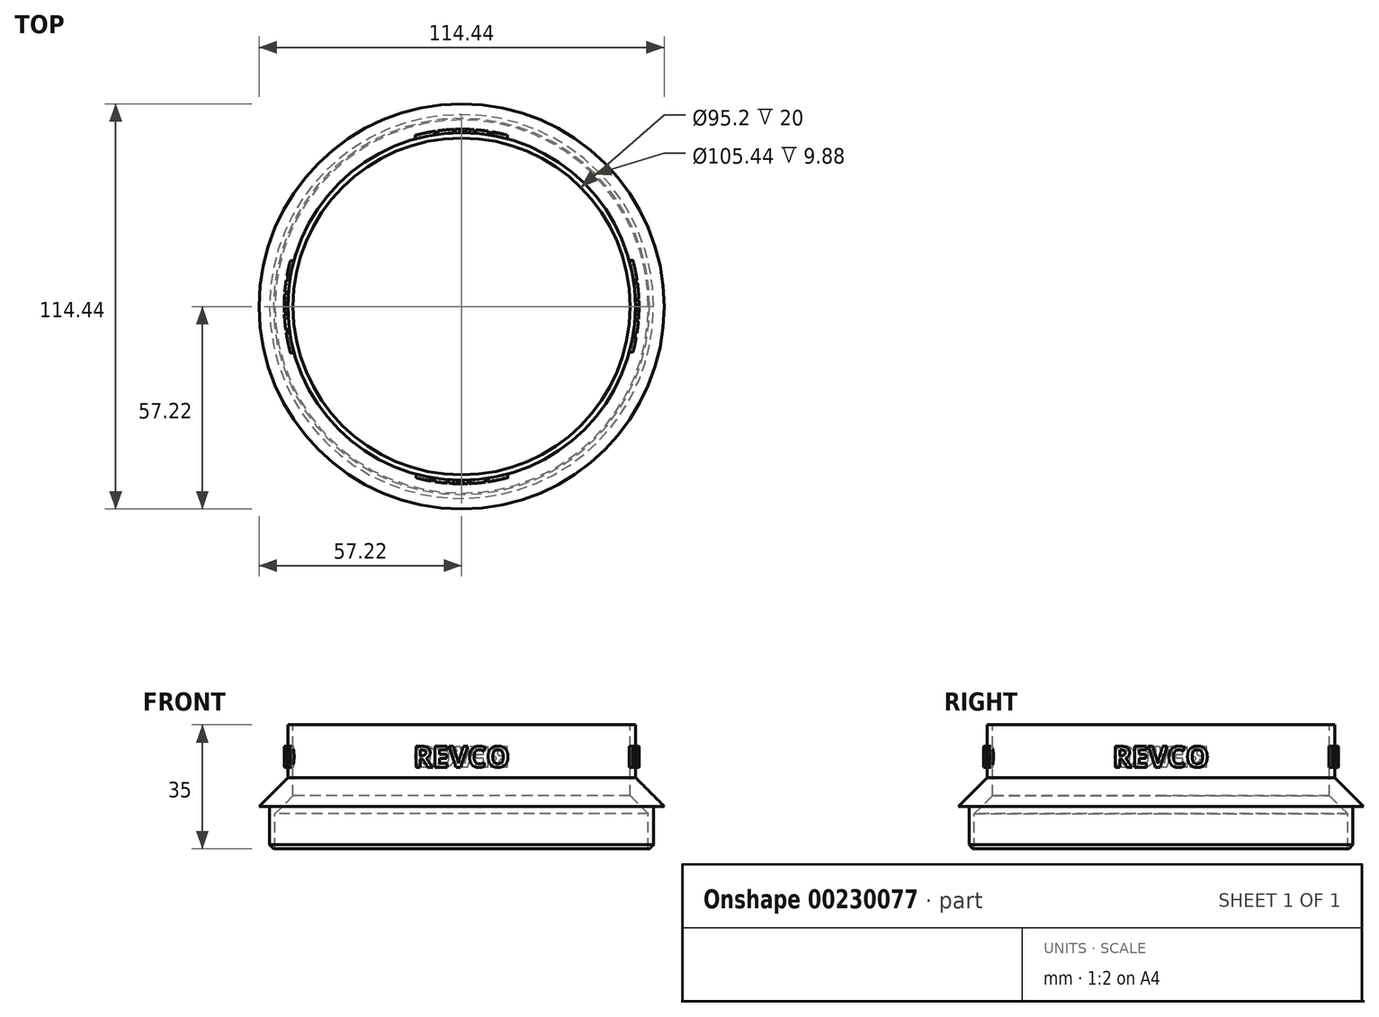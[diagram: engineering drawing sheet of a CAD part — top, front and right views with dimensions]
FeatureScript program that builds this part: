
annotation { "Feature Type Name" : "Feature", "Feature Type Description" : "" }
export const myFeature = defineFeature(function(context is Context, id is Id, definition is map)
    precondition{}
    {
        {
            var Q0;
            Q0=qCreatedBy(makeId("Front.planeOp"),FACE);
            var sketch = newSketch(context, id + "F0", { "sketchPlane" : qUnion([Q0])});
            skLineSegment(sketch, "E0", {"start": v(0, 55.93) * mm, "end": v(0, -56.28) * mm, "construction": true});
            skLineSegment(sketch, "E1.bottom", {"start": v(47.6, 20) * mm, "end": v(49.1, 20) * mm});
            skLineSegment(sketch, "E1.top", {"start": v(47.6, 0) * mm, "end": v(49.1, 0) * mm});
            skLineSegment(sketch, "E1.left", {"start": v(47.6, 20) * mm, "end": v(47.6, 0) * mm});
            skLineSegment(sketch, "E1.right", {"start": v(49.1, 20) * mm, "end": v(49.1, 0) * mm});
            skLineSegment(sketch, "E2.bottom", {"start": v(52.72, 0) * mm, "end": v(54.22, 0) * mm});
            skLineSegment(sketch, "E2.top", {"start": v(52.72, -15) * mm, "end": v(54.22, -15) * mm});
            skLineSegment(sketch, "E2.left", {"start": v(52.72, 0) * mm, "end": v(52.72, -15) * mm});
            skLineSegment(sketch, "E2.right", {"start": v(54.22, 0) * mm, "end": v(54.22, -15) * mm});
            skLineSegment(sketch, "E3", {"start": v(47.6, 0) * mm, "end": v(52.72, -5.12) * mm});
            skLineSegment(sketch, "E4", {"start": v(49.1, 5.12) * mm, "end": v(54.22, 0) * mm});
            skLineSegment(sketch, "E5", {"start": v(54.22, 0) * mm, "end": v(57.22, -3) * mm});
            skLineSegment(sketch, "E6", {"start": v(57.22, -3) * mm, "end": v(54.22, -3) * mm});
            skLineSegment(sketch, "E7", {"start": v(50.1, 18.25) * mm, "end": v(50.1, 5.74) * mm});
            skSolve(sketch);
        }
        {
            var Q0;
            {var subQ1=sQuery(id+"F0.wireOp",EDGE,"E1.bottom");Q0=makeQuery(id+"F0.imprint","IMPRINT",FACE,{"disambiguationData":[TD([[makeQuery(id+"F0.imprint","IMPRINT",EDGE,{"derivedFrom":subQ1}),-1.0]])]});}
            var Q1;
            {var subQ0=sQuery(id+"F0.wireOp",EDGE,"E5");Q1=makeQuery(id+"F0.imprint","IMPRINT",FACE,{"disambiguationData":[TD([[makeQuery(id+"F0.imprint","IMPRINT",EDGE,{"derivedFrom":subQ0}),-1.0]])]});}
            var Q2;
            {var subQ5=sQuery(id+"F0.wireOp",EDGE,"E1.top");Q2=makeQuery(id+"F0.imprint","IMPRINT",FACE,{"disambiguationData":[TD([[makeQuery(id+"F0.imprint","IMPRINT",EDGE,{"derivedFrom":subQ5}),-1.0]])]});}
            var Q3;
            {var subQ3=sQuery(id+"F0.wireOp",EDGE,"E2.bottom");Q3=makeQuery(id+"F0.imprint","IMPRINT",FACE,{"disambiguationData":[TD([[makeQuery(id+"F0.imprint","IMPRINT",EDGE,{"derivedFrom":subQ3}),-1.0]])]});}
            var Q4;
            Q4=sQuery(id+"F0.wireOp",EDGE,"E0");
            revolve(context, id + "F1", {"entities" : qUnion([Q0, Q1, Q2, Q3]), "axis" : qUnion([Q4]), "revolveType" : RevolveType.FULL});
        }
        {
            var Q0;
            Q0=makeQuery(id+"F1.opRevolve","SWEPT_EDGE",EDGE,{"disambiguationData":[OSD([sQuery(id+"F0.wireOp",EDGE,"E2.top"),sQuery(id+"F0.wireOp",EDGE,"E2.right")])]});
            chamfer(context, id + "F2", {"entities" : qUnion([Q0]), "width" : 1.1 * mm, "tangentPropagation" : true});
        }
        {
            var Q0;
            Q0 = qSketchRegion(id + "F0", true);
            var Q1;
            Q1=sQuery(id+"F0.wireOp",EDGE,"E7");
            var Q2;
            Q2=sQuery(id+"F0.wireOp",EDGE,"E0");
            revolve(context, id + "F3", {"bodyType" : ToolBodyType.SURFACE, "entities" : qUnion([Q0]), "surfaceEntities" : qUnion([Q1]), "axis" : qUnion([Q2]), "revolveType" : RevolveType.SYMMETRIC, "angle" : 1 * degree});
        }
        {
            var Q0;
            Q0=qCreatedBy(makeId("Right.planeOp"),FACE);
            cPlane(context, id + "F4", {"entities" : qUnion([Q0]), "cplaneType" : CPlaneType.OFFSET, "offset" : 60 * mm, "width" : 150 * mm, "height" : 150 * mm});
        }
        {
            var Q0;
            Q0=qCreatedBy(id+"F4.planeOp",FACE);
            var sketch = newSketch(context, id + "F5", { "sketchPlane" : qUnion([Q0])});
            skText(sketch, "E8", { "text": "REVCO", "fontName": "OpenSans-Bold.ttf"});
            const initialGuessF5  = {"E8": [-0.01364, 0.00805, 1, 0, 0.00593]};
            skSetInitialGuess(sketch, initialGuessF5);
            skSolve(sketch);
        }
        {
            var Q0;
            Q0 = qSketchRegion(id + "F5", true);
            var Q1;
            Q1=makeQuery(id+"F1.opRevolve","SWEPT_FACE",FACE,{"disambiguationData":[OSD([sQuery(id+"F0.wireOp",EDGE,"E1.right")])]});
            var Q2;
            Q2=makeQuery(id+"F3.opRevolve","SWEPT_FACE",FACE,{"disambiguationData":[OSD([sQuery(id+"F0.wireOp",EDGE,"E7")])]});
            extrude(context, id + "F6", {"entities" : qUnion([Q0]), "endBound" : BoundingType.UP_TO_SURFACE, "oppositeDirection" : true, "endBoundEntityFace" : qUnion([Q1]), "depth" : 25 * mm, "hasSecondDirection" : true, "secondDirectionBound" : SecondDirectionBoundingType.UP_TO_SURFACE, "secondDirectionOppositeDirection" : true, "secondDirectionBoundEntityFace" : qUnion([Q2]), "secondDirectionDepth" : 25 * mm});
        }
        {
            var Q0;
            Q0=makeQuery(id+"F6.opExtrude","SWEPT_BODY",BODY,{"disambiguationData":[OSD([sQuery(id+"F5.wireOp",EDGE,"E8.sketch_text.stroke-0"),sQuery(id+"F5.wireOp",EDGE,"E8.sketch_text.stroke-1"),sQuery(id+"F5.wireOp",EDGE,"E8.sketch_text.stroke-2"),sQuery(id+"F5.wireOp",EDGE,"E8.sketch_text.stroke-3"),sQuery(id+"F5.wireOp",EDGE,"E8.sketch_text.stroke-4"),sQuery(id+"F5.wireOp",EDGE,"E8.sketch_text.stroke-5"),sQuery(id+"F5.wireOp",EDGE,"E8.sketch_text.stroke-6"),sQuery(id+"F5.wireOp",EDGE,"E8.sketch_text.stroke-7"),sQuery(id+"F5.wireOp",EDGE,"E8.sketch_text.stroke-8"),sQuery(id+"F5.wireOp",EDGE,"E8.sketch_text.stroke-9"),sQuery(id+"F5.wireOp",EDGE,"E8.sketch_text.stroke-10"),sQuery(id+"F5.wireOp",EDGE,"E8.sketch_text.stroke-11"),sQuery(id+"F5.wireOp",EDGE,"E8.sketch_text.stroke-12"),sQuery(id+"F5.wireOp",EDGE,"E8.sketch_text.stroke-13"),sQuery(id+"F5.wireOp",EDGE,"E8.sketch_text.stroke-14"),sQuery(id+"F5.wireOp",EDGE,"E8.sketch_text.stroke-15"),sQuery(id+"F5.wireOp",EDGE,"E8.sketch_text.stroke-16"),sQuery(id+"F5.wireOp",EDGE,"E8.sketch_text.stroke-17"),sQuery(id+"F5.wireOp",EDGE,"E8.sketch_text.stroke-18")])]});
            var Q1;
            Q1=makeQuery(id+"F6.opExtrude","SWEPT_BODY",BODY,{"disambiguationData":[OSD([sQuery(id+"F5.wireOp",EDGE,"E8.sketch_text.stroke-19"),sQuery(id+"F5.wireOp",EDGE,"E8.sketch_text.stroke-20"),sQuery(id+"F5.wireOp",EDGE,"E8.sketch_text.stroke-21"),sQuery(id+"F5.wireOp",EDGE,"E8.sketch_text.stroke-22"),sQuery(id+"F5.wireOp",EDGE,"E8.sketch_text.stroke-23"),sQuery(id+"F5.wireOp",EDGE,"E8.sketch_text.stroke-24"),sQuery(id+"F5.wireOp",EDGE,"E8.sketch_text.stroke-25"),sQuery(id+"F5.wireOp",EDGE,"E8.sketch_text.stroke-26"),sQuery(id+"F5.wireOp",EDGE,"E8.sketch_text.stroke-27"),sQuery(id+"F5.wireOp",EDGE,"E8.sketch_text.stroke-28"),sQuery(id+"F5.wireOp",EDGE,"E8.sketch_text.stroke-29"),sQuery(id+"F5.wireOp",EDGE,"E8.sketch_text.stroke-30")])]});
            var Q2;
            Q2=makeQuery(id+"F6.opExtrude","SWEPT_BODY",BODY,{"disambiguationData":[OSD([sQuery(id+"F5.wireOp",EDGE,"E8.sketch_text.stroke-31"),sQuery(id+"F5.wireOp",EDGE,"E8.sketch_text.stroke-32"),sQuery(id+"F5.wireOp",EDGE,"E8.sketch_text.stroke-33"),sQuery(id+"F5.wireOp",EDGE,"E8.sketch_text.stroke-34"),sQuery(id+"F5.wireOp",EDGE,"E8.sketch_text.stroke-35"),sQuery(id+"F5.wireOp",EDGE,"E8.sketch_text.stroke-36"),sQuery(id+"F5.wireOp",EDGE,"E8.sketch_text.stroke-37"),sQuery(id+"F5.wireOp",EDGE,"E8.sketch_text.stroke-38"),sQuery(id+"F5.wireOp",EDGE,"E8.sketch_text.stroke-39"),sQuery(id+"F5.wireOp",EDGE,"E8.sketch_text.stroke-40")])]});
            var Q3;
            Q3=makeQuery(id+"F6.opExtrude","SWEPT_BODY",BODY,{"disambiguationData":[OSD([sQuery(id+"F5.wireOp",EDGE,"E8.sketch_text.stroke-41"),sQuery(id+"F5.wireOp",EDGE,"E8.sketch_text.stroke-42"),sQuery(id+"F5.wireOp",EDGE,"E8.sketch_text.stroke-43"),sQuery(id+"F5.wireOp",EDGE,"E8.sketch_text.stroke-44"),sQuery(id+"F5.wireOp",EDGE,"E8.sketch_text.stroke-45"),sQuery(id+"F5.wireOp",EDGE,"E8.sketch_text.stroke-46"),sQuery(id+"F5.wireOp",EDGE,"E8.sketch_text.stroke-47"),sQuery(id+"F5.wireOp",EDGE,"E8.sketch_text.stroke-48"),sQuery(id+"F5.wireOp",EDGE,"E8.sketch_text.stroke-49"),sQuery(id+"F5.wireOp",EDGE,"E8.sketch_text.stroke-50"),sQuery(id+"F5.wireOp",EDGE,"E8.sketch_text.stroke-51"),sQuery(id+"F5.wireOp",EDGE,"E8.sketch_text.stroke-52"),sQuery(id+"F5.wireOp",EDGE,"E8.sketch_text.stroke-53"),sQuery(id+"F5.wireOp",EDGE,"E8.sketch_text.stroke-54"),sQuery(id+"F5.wireOp",EDGE,"E8.sketch_text.stroke-55")])]});
            var Q4;
            Q4=makeQuery(id+"F6.opExtrude","SWEPT_BODY",BODY,{"disambiguationData":[OSD([sQuery(id+"F5.wireOp",EDGE,"E8.sketch_text.stroke-56"),sQuery(id+"F5.wireOp",EDGE,"E8.sketch_text.stroke-57"),sQuery(id+"F5.wireOp",EDGE,"E8.sketch_text.stroke-58"),sQuery(id+"F5.wireOp",EDGE,"E8.sketch_text.stroke-59"),sQuery(id+"F5.wireOp",EDGE,"E8.sketch_text.stroke-60"),sQuery(id+"F5.wireOp",EDGE,"E8.sketch_text.stroke-61"),sQuery(id+"F5.wireOp",EDGE,"E8.sketch_text.stroke-62"),sQuery(id+"F5.wireOp",EDGE,"E8.sketch_text.stroke-63"),sQuery(id+"F5.wireOp",EDGE,"E8.sketch_text.stroke-64"),sQuery(id+"F5.wireOp",EDGE,"E8.sketch_text.stroke-65"),sQuery(id+"F5.wireOp",EDGE,"E8.sketch_text.stroke-66"),sQuery(id+"F5.wireOp",EDGE,"E8.sketch_text.stroke-67"),sQuery(id+"F5.wireOp",EDGE,"E8.sketch_text.stroke-68"),sQuery(id+"F5.wireOp",EDGE,"E8.sketch_text.stroke-69")])]});
            var Q5;
            Q5=sQuery(id+"F0.wireOp",EDGE,"E0");
            circularPattern(context, id + "F7", {"entities" : qUnion([Q0, Q1, Q2, Q3, Q4]), "axis" : qUnion([Q5]), "angle" : 360 * degree, "instanceCount" : 4, "equalSpace" : true});
        }
    });
